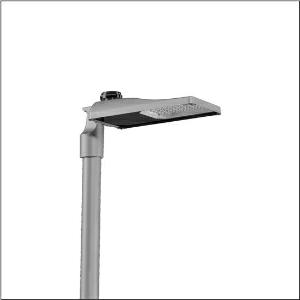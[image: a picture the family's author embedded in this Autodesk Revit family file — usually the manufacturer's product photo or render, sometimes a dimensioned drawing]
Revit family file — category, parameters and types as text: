
# Revit family: streetlight_sl_31_mini___st1_0a_5xh2d35n08ga_ac29
name_source: partatom
category: Lighting Fixtures
units: mm (PartAtom-declared; Revit-internal decimal feet)

## family parameters
Cut with Voids When Loaded = No
Host = Face
Light Source = No
Part Type = Normal
Room Calculation Point = No
Round Connector Dimension = Use Diameter
Shared = No

## types (1)
- --- (1 x LED, 5710 lm, 37.3 W, 3000K)
    Apparent Load = 37 VA
    CIE Flux Codes = 37 72 97 100 100
    Color Rendering = 70
    Color Temperature = 3000K
    Default Elevation = 1800 mm
    Description = Streetlight SL 31 mini, mast luminaire, primary light control with lens, of PMMA, primary optical cover: cover, of toughened safety glass, transparent, light distribution: ST1.0a, light emission: direct distribution, primary light characteristic: asymmetric, installation type: post-top, side-entry, LED, High Power LED, rated luminous flux: 5.710lm, luminous efficacy: 153lm/W, light colour: 730, colour temperature: 3000K, control: presetting dimming linear, flexible luminous flux parameterisation, time-dependent luminous flux control, constant luminous flux control, intelligent temperature release in ECG and LED module, overheat protection, with cable H07RN-F 3x 1.5mm², mains connection: 220..240V, AC, 50/60Hz, connection cable pre-assembled, cable length: 6,5m, start of lifetime: 37W, end of service life: 39W, reduction: 18W, luminaire housing, of diecast aluminium, powder-coated, Siteco® metallic grey (DB 702S), corrosivity category C5 high according to DIN EN ISO 12944, no sealing on luminaire upper side, inclination: -15°..+20° (post-top) | -20°..+20° (side-entry), adjustable in 5° steps, mast flange (76/60mm) included as standard, multi-level sealing system, sealing non-destructively replaceable, protection rating (complete): IP66, insulation class (complete): insulation class I (protective earthing), certification: CE, ENEC, ENEC+, VDE, UKCA, impact resistance: IK09, permissible operating ambient temperature for outdoor applications: -40..+50°C, standard-compliant lighting for roads and squares, packaging unit: 1 piece

Light Distribution: ST1.0a
    Height = 76 mm
    Lamp = 1 x LED
    Lamp Light Flux = 5710 lm
    Lamp Power = 37.3 W
    Lamp count = 1
    Length = 547 mm
    Luminous efficacy = 153 lm/W
    Manufacturer = Siteco
    ModVariant = No
    Model = 5XH2D35N08GA
    Number of Poles = 1
    OnlyDefault = Yes
    Power Factor = 1
    Product Name = Streetlight SL 31 mini | ST1.0a
    Product group = mast luminaire | pylon top
    ProductGroupID = 6100
    Protection Class = Protection class I
    Protection Degree = IP 66
    RLX_Detail_Level = 1
    RLX_Emergency_Light_Flux = 0 lm
    RLX_Emergency_Type = 0
    RLX_Emergency_Type_DB = No
    RlxData = <blob elided: 40369 chars, md5=727d56a4>
    Socket = socket
    Standby Power = 0 W
    System Light Flux = 5710 lm
    System Power = 37 W
    Type Comments = factory setting: luminous flux: 100 % | dim-lin: 254 | 386 mA
    Type Image = l_1300322.jpg
    URL = http://relux.com
    VarID = @adj_012689
    Voltage = 0 V
    Weight = 0.00 kg
    Width = 265 mm

## geometry (parser evidence)
native form markers: Blend x4, Sweep x10
no freeform markers — native parametric forms only
